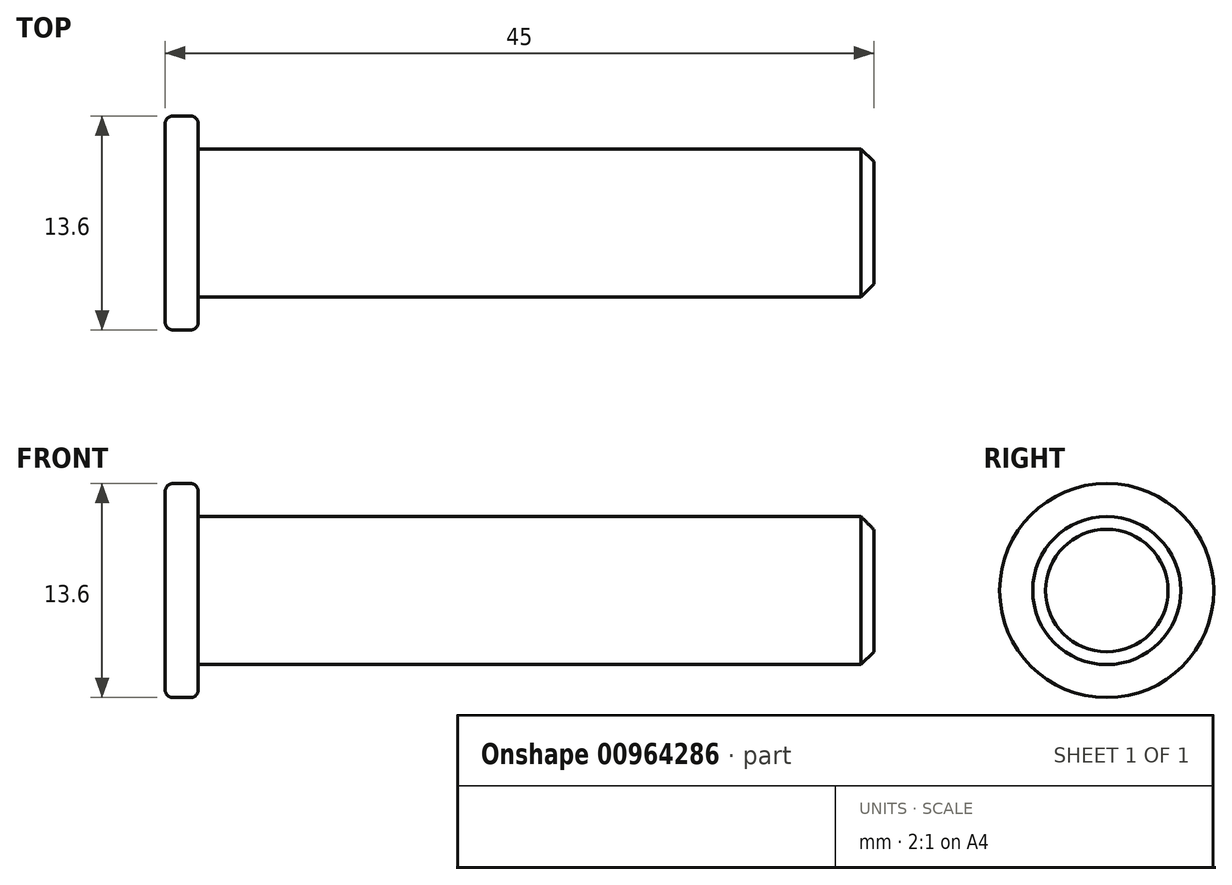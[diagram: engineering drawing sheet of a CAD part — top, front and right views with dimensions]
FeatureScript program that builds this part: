
annotation { "Feature Type Name" : "Feature", "Feature Type Description" : "" }
export const myFeature = defineFeature(function(context is Context, id is Id, definition is map)
    precondition{}
    {
        {
            var Q0;
            Q0=qCreatedBy(makeId("Front.planeOp"),FACE);
            var sketch = newSketch(context, id + "F0", { "sketchPlane" : qUnion([Q0])});
            skLineSegment(sketch, "E0", {"start": v(0, 0) * mm, "end": v(45, 0) * mm});
            skLineSegment(sketch, "E1", {"start": v(45, 0) * mm, "end": v(45, 4.7) * mm});
            skLineSegment(sketch, "E2", {"start": v(45, 4.7) * mm, "end": v(2.1, 4.7) * mm});
            skLineSegment(sketch, "E3", {"start": v(2.1, 4.7) * mm, "end": v(2.1, 6.8) * mm});
            skLineSegment(sketch, "E4", {"start": v(2.1, 6.8) * mm, "end": v(0, 6.8) * mm});
            skLineSegment(sketch, "E5", {"start": v(0, 6.8) * mm, "end": v(0, 0) * mm});
            skSolve(sketch);
        }
        {
            var Q0;
            Q0 = qSketchRegion(id + "F0", true);
            var Q1;
            Q1=sQuery(id+"F0.wireOp",EDGE,"E0");
            revolve(context, id + "F1", {"surfaceOperationType" : NewSurfaceOperationType.NEW, "entities" : qUnion([Q0]), "axis" : qUnion([Q1]), "revolveType" : RevolveType.FULL});
        }
        {
            var Q0;
            Q0=makeQuery(id+"F1.opRevolve","SWEPT_EDGE",EDGE,{"disambiguationData":[OSD([sQuery(id+"F0.wireOp",EDGE,"E1"),sQuery(id+"F0.wireOp",EDGE,"E2")])]});
            chamfer(context, id + "F2", {"entities" : qUnion([Q0]), "chamferType" : ChamferType.OFFSET_ANGLE, "width" : .81 * mm, "oppositeDirection" : false, "angle" : 45 * degree, "tangentPropagation" : true});
        }
        {
            var Q0;
            Q0=makeQuery(id+"F1.opRevolve","SWEPT_FACE",FACE,{"disambiguationData":[OSD([sQuery(id+"F0.wireOp",EDGE,"E4")])]});
            fillet(context, id + "F3", {"entities" : qUnion([Q0]), "radius" : .5 * mm, "tangentPropagation" : true, "allowEdgeOverflow" : false});
        }
    });
